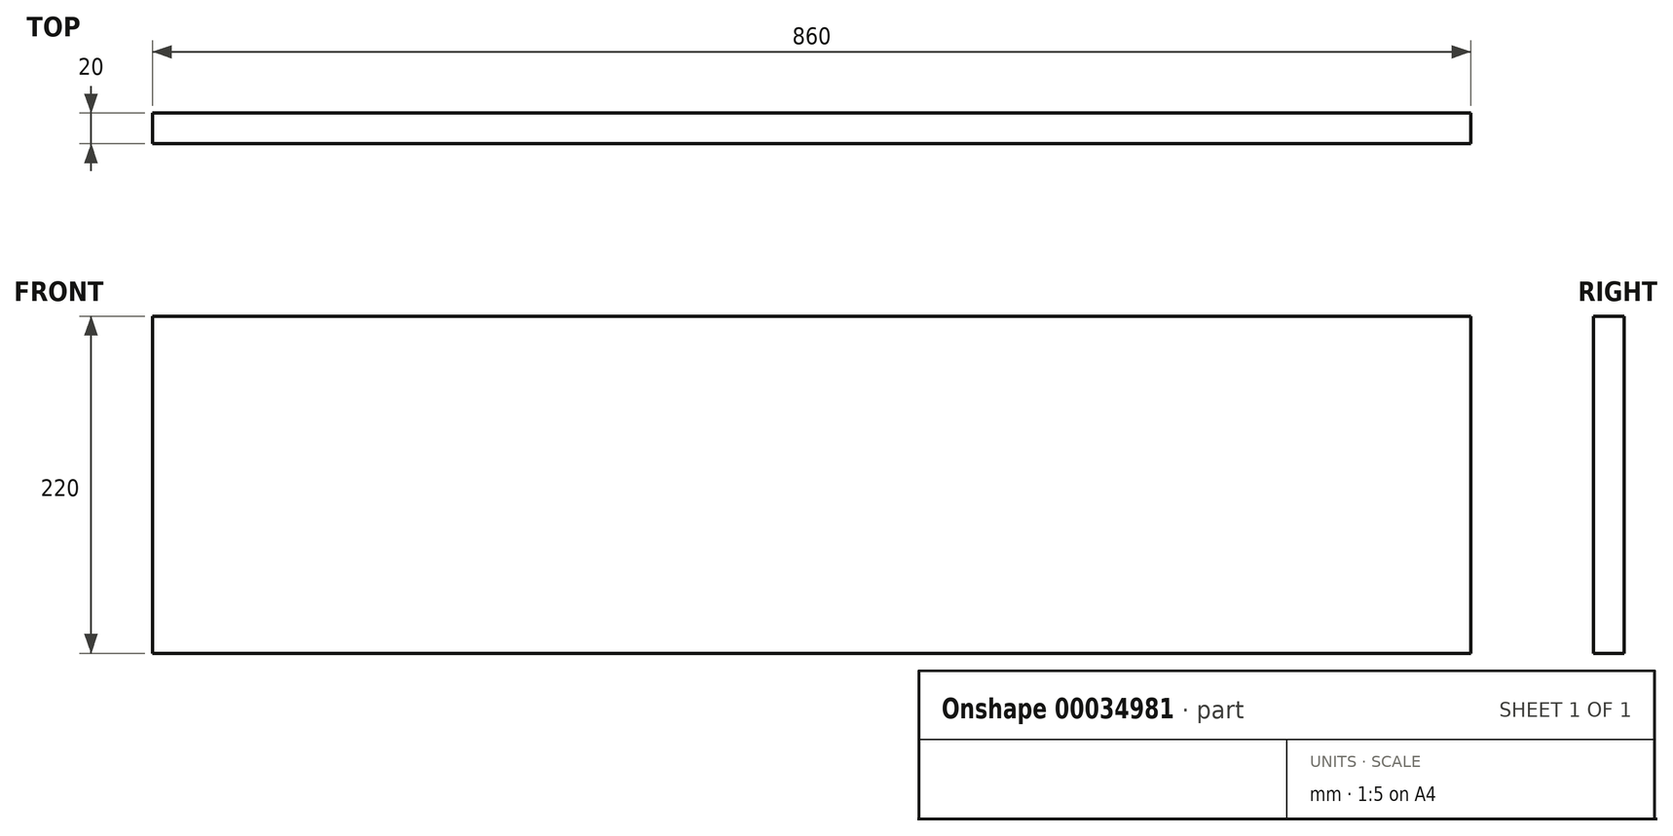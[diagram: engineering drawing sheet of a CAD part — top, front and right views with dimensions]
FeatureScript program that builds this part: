
annotation { "Feature Type Name" : "Feature", "Feature Type Description" : "" }
export const myFeature = defineFeature(function(context is Context, id is Id, definition is map)
    precondition{}
    {
        {
            var Q0;
            Q0=qCreatedBy(makeId("Front.planeOp"),FACE);
            var sketch = newSketch(context, id + "F0", { "sketchPlane" : qUnion([Q0])});
            skLineSegment(sketch, "E0.bottom", {"start": v(0, 0) * mm, "end": v(860, 0) * mm});
            skLineSegment(sketch, "E0.top", {"start": v(0, 220) * mm, "end": v(860, 220) * mm});
            skLineSegment(sketch, "E0.left", {"start": v(0, 0) * mm, "end": v(0, 220) * mm});
            skLineSegment(sketch, "E0.right", {"start": v(860, 0) * mm, "end": v(860, 220) * mm});
            skSolve(sketch);
        }
        {
            var Q0;
            Q0=makeQuery(id+"F0.imprint","IMPRINT",FACE,{"disambiguationData":[TD([[makeQuery(id+"F0.imprint","IMPRINT",EDGE,{"derivedFrom":sQuery(id+"F0.wireOp",EDGE,"E0.bottom")}),1.0]])]});
            extrude(context, id + "F1", {"entities" : qUnion([Q0]), "depth" : 20 * mm});
        }
    });
